# Revit family: ForteHome_РадиаторСекционныйБиметаллический_HalsenBS350х80 1
name_source: partatom
category: Оборудование
revit_build: Autodesk Revit 2017 (Build: 20170118_1100(x64)
units: mm (PartAtom-declared; Revit-internal decimal feet)

## family parameters
Всегда вертикально = Да
Заголовок OmniClass = Climate Control (HVAC)
Номер OmniClass = 23.75.00.00
Общий = Нет
Основа = Стена
При загрузке вырезать с полостями = Нет
Размер круглого соединителя = Использовать диаметр
Тип детали = Нормальный
Точка расчета площади = Нет

## types (5) — shared parameters
ADSK_URL документации изделия = https://fortehome.ru
ADSK_URL страницы изделия = https://fortehome.ru
ADSK_Версия Revit = 2017
ADSK_Версия семейства = 1
ADSK_Единица измерения = шт
ADSK_Завод-изготовитель = Forte Home - Россия
ADSK_Размер_Высота = 415 мм
ADSK_Размер_Глубина = 78 мм
pH_теплоносителя = 6,5-9
Группа модели = Продукт - официальная версия производителя
ЕмкостьСекции литров = 0.16
Изготовитель = BIM модель разработана НПО ИНКОМИС
ИспытательноеДавление атм = 38
Комментарии к типоразмеру = Все права на BIM модель принадлежат Форте Хоум ГмбХ
МаксимальнаяТеператураТеплоносителя = 110°С
МассаСекции = 1.3
МежосевоеРасстояние = 350 мм
МощностьСекцииНоминальная (ПриТепловомНапоре 70°С) паспортные данные = 127 Вт
Описание = Отопительные приборы
ОтЗадСтенкиРадиатораДоСоединителей = 39 мм
ОтНизаРадиатораДоВерхВыпуска = 385 мм
ОтНизаРадиатораДоНижнегоВыпуска = 35 мм
РабочееДавление атм = 25
ШиринаСекции = 82 мм

## per-type parameters (varying)
| type | ADSK_Марка | ADSK_Масса | ADSK_Масса_Текст | ADSK_Наименование | ADSK_Наименование краткое | ADSK_Размер_Ширина | ДлинаСоединителей | КоличествоСекций | МощностьРадиатораНоминальная |
| 8 секций с монтажным комплектом и доп кронштейнами | ОП-BS350х80-8 | 10.4 | 10,4 | Радиатор восьми секционный биметаллический HalsenBS350х80-8 | ОП-HalsenBS350х80-8 | 656 мм | 328 мм | 8 | 1016 Вт |
| 4 секции с монтажным комплектом и доп кронштейнами | ОП-BS350х80-4 | 5.2 | 5,2 | Радиатор четырех секционный биметаллический HalsenBS350х80-4 | ОП-HalsenBS350х80-4 | 328 мм | 164 мм | 4 | 508 Вт |
| 6 секций с монтажным комплектом и доп кронштейнами | ОП-BS350х80-6 | 7.8 | 7,8 | Радиатор шести секционный биметаллический HalsenBS350х80-6 | ОП-HalsenBS350х80-6 | 492 мм | 246 мм | 6 | 762 Вт |
| 10 секций с монтажным комплектом и доп кронштейнами | ОП-BS350х80-10 | 13 | 13 | Радиатор десяти секционный биметаллический HalsenBS350х80-10 | ОП-HalsenBS350х80-10 | 820 мм | 410 мм | 10 | 1270 Вт |
| 12 секций с монтажным комплектом и доп кронштейнами | ОП-BS350х80-12 | 15.6 | 15,6 | Радиатор двенадцати секционный биметаллический HalsenBS350х80-12 | ОП-HalsenBS350х80-12 | 984 мм | 492 мм | 12 | 1524 Вт |
